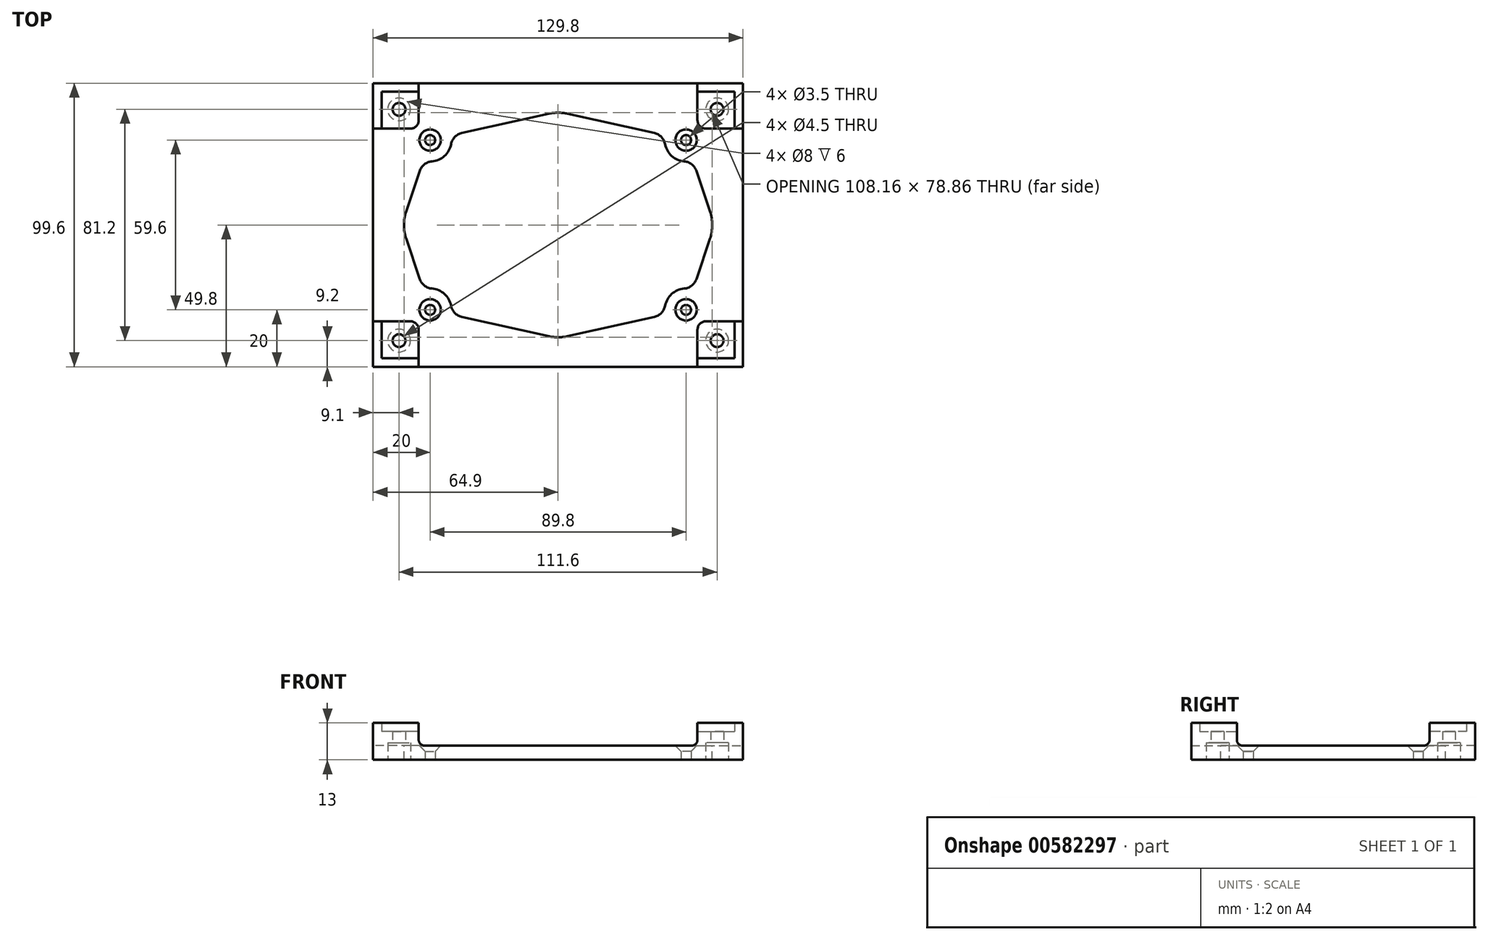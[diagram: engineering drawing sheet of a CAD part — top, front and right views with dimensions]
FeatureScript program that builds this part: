
annotation { "Feature Type Name" : "Feature", "Feature Type Description" : "" }
export const myFeature = defineFeature(function(context is Context, id is Id, definition is map)
    precondition{}
    {
        {
            var Q0;
            Q0=qCreatedBy(makeId("Top.planeOp"),FACE);
            var sketch = newSketch(context, id + "F0", { "sketchPlane" : qUnion([Q0])});
            skCircle(sketch, "E0", {"center": v(55.8, 40.6) * mm, "radius": 2.25 * mm});
            skCircle(sketch, "E1", {"center": v(55.8, 40.6) * mm, "radius": 4 * mm});
            skCircle(sketch, "E2", {"center": v(44.9, 29.8) * mm, "radius": 1.75 * mm});
            skLineSegment(sketch, "E3", {"start": v(0, 45.8) * mm, "end": v(60.9, 45.8) * mm, "construction": true});
            skLineSegment(sketch, "E4", {"start": v(60.9, 45.8) * mm, "end": v(60.9, 0) * mm, "construction": true});
            skLineSegment(sketch, "E5", {"start": v(48.9, 49.8) * mm, "end": v(48.9, 46.8) * mm});
            skLineSegment(sketch, "E6", {"start": v(48.9, 46.8) * mm, "end": v(61.9, 46.8) * mm});
            skLineSegment(sketch, "E7", {"start": v(61.9, 46.8) * mm, "end": v(61.9, 33.8) * mm});
            skLineSegment(sketch, "E8", {"start": v(61.9, 33.8) * mm, "end": v(64.9, 33.8) * mm});
            skLineSegment(sketch, "E9", {"start": v(64.9, 33.8) * mm, "end": v(64.9, 49.8) * mm});
            skLineSegment(sketch, "E10", {"start": v(64.9, 49.8) * mm, "end": v(48.9, 49.8) * mm});
            skLineSegment(sketch, "E11", {"start": v(48.9, 49.8) * mm, "end": v(0, 49.8) * mm});
            skLineSegment(sketch, "E12", {"start": v(64.9, 33.8) * mm, "end": v(64.9, 0) * mm});
            skLineSegment(sketch, "E13", {"start": v(44.9, 29.8) * mm, "end": v(0, 39.8) * mm});
            skLineSegment(sketch, "E14", {"start": v(44.9, 29.8) * mm, "end": v(54.9, 0) * mm});
            skArc(sketch, "E15", {"start": v(37.58, 31.43) * mm, "mid": v(39.88, 24.23) * mm, "end": v(47.29, 22.69) * mm});
            skLineSegment(sketch, "E16", {"start": v(0, 49.8) * mm, "end": v(0, 39.8) * mm});
            skLineSegment(sketch, "E17", {"start": v(54.9, 0) * mm, "end": v(64.9, 0) * mm});
            skLineSegment(sketch, "E18", {"start": v(48.9, 46.8) * mm, "end": v(48.9, 33.8) * mm});
            skLineSegment(sketch, "E19", {"start": v(48.9, 33.8) * mm, "end": v(61.9, 33.8) * mm});
            skSolve(sketch);
        }
        {
            var Q0;
            Q0=makeQuery(id+"F0.imprint","IMPRINT",FACE,{"disambiguationData":[TD([[makeQuery(id+"F0.imprint","IMPRINT",EDGE,{"derivedFrom":sQuery(id+"F0.wireOp",EDGE,"E5")}),-1.0]])]});
            var Q1;
            {var subQ5=sQuery(id+"F0.wireOp",EDGE,"E15");Q1=makeQuery(id+"F0.imprint","IMPRINT",FACE,{"disambiguationData":[TD([[makeQuery(id+"F0.imprint","IMPRINT",EDGE,{"derivedFrom":subQ5}),1.0]])]});}
            extrude(context, id + "F1", {"entities" : qUnion([Q0, Q1]), "depth" : 5 * mm, "offsetDistance" : 25 * mm});
        }
        {
            var Q0;
            Q0=makeQuery(id+"F0.imprint","IMPRINT",FACE,{"disambiguationData":[TD([[makeQuery(id+"F0.imprint","IMPRINT",EDGE,{"derivedFrom":sQuery(id+"F0.wireOp",EDGE,"E1")}),-1.0]])]});
            var Q1;
            Q1=makeQuery(id+"F0.imprint","IMPRINT",FACE,{"disambiguationData":[TD([[makeQuery(id+"F0.imprint","IMPRINT",EDGE,{"derivedFrom":sQuery(id+"F0.wireOp",EDGE,"E0")}),-1.0]])]});
            extrude(context, id + "F2", {"entities" : qUnion([Q0, Q1]), "operationType" : NewBodyOperationType.ADD, "depth" : 10 * mm, "offsetDistance" : 25 * mm});
        }
        {
            var Q0;
            Q0=makeQuery(id+"F0.imprint","IMPRINT",FACE,{"disambiguationData":[TD([[makeQuery(id+"F0.imprint","IMPRINT",EDGE,{"derivedFrom":sQuery(id+"F0.wireOp",EDGE,"E5")}),1.0]])]});
            extrude(context, id + "F3", {"entities" : qUnion([Q0]), "operationType" : NewBodyOperationType.ADD, "depth" : 13 * mm, "offsetDistance" : 25 * mm});
        }
        {
            var Q0;
            Q0=makeQuery(id+"F0.imprint","IMPRINT",FACE,{"disambiguationData":[TD([[makeQuery(id+"F0.imprint","IMPRINT",EDGE,{"derivedFrom":sQuery(id+"F0.wireOp",EDGE,"E0")}),-1.0]])]});
            extrude(context, id + "F4", {"entities" : qUnion([Q0]), "operationType" : NewBodyOperationType.REMOVE, "depth" : 6 * mm, "offsetDistance" : 25 * mm});
        }
        {
            var Q0;
            Q0=makeQuery(id+"F1.opExtrude","CAP_EDGE",EDGE,{"disambiguationData":[OSD([sQuery(id+"F0.wireOp",EDGE,"E2")])],"isStart":false});
            chamfer(context, id + "F5", {"entities" : qUnion([Q0]), "width" : 2 * mm, "tangentPropagation" : true});
        }
        {
            var Q0;
            Q0=makeQuery(id+"F2.opExtrude","SWEPT_EDGE",EDGE,{"disambiguationData":[OSD([sQuery(id+"F0.wireOp",EDGE,"E18"),sQuery(id+"F0.wireOp",EDGE,"E19")])]});
            fillet(context, id + "F6", {"entities" : qUnion([Q0]), "radius" : 3 * mm, "tangentPropagation" : true, "allowEdgeOverflow" : false});
        }
        {
            var Q0;
            {var subQ0=sQuery(id+"F0.wireOp",EDGE,"E19");var subQ1=sQuery(id+"F0.wireOp",EDGE,"E8");var subQ3=makeQuery(id+"F1.opExtrude","CAP_EDGE",EDGE,{"disambiguationData":[OSD([subQ1,subQ0])],"isStart":false});Q0=makeQuery(id+"F3.boolean.opBoolean","MERGE",EDGE,{"derivedFrom":[makeQuery(id+"F2.boolean.opBoolean","SPLIT",EDGE,{"disambiguationData":[topologyDisambiguationEdgeConnected([makeQuery(id+"F1.opExtrude","SWEPT_FACE",FACE,{"disambiguationData":[OSD([subQ1,subQ0])]})])],"derivedFrom":subQ3}),makeQuery(id+"F2.boolean.opBoolean","SPLIT",EDGE,{"disambiguationData":[topologyDisambiguationEdgeConnected([makeQuery(id+"F2.opExtrude","SWEPT_FACE",FACE,{"disambiguationData":[OSD([subQ0])]})])],"derivedFrom":subQ3})]});}
            var Q1;
            {var subQ0=sQuery(id+"F0.wireOp",EDGE,"E19");var subQ1=sQuery(id+"F0.wireOp",EDGE,"E18");Q1=makeQuery(id+"F6.opFillet","BLEND_EDGE",EDGE,{"blendedFrom":[makeQuery(id+"F2.opExtrude","SWEPT_EDGE",EDGE,{"disambiguationData":[OSD([subQ1,subQ0])]}),makeQuery(id+"F1.opExtrude","CAP_FACE",FACE,{"disambiguationData":[OSD([sQuery(id+"F0.wireOp",EDGE,"E2"),sQuery(id+"F0.wireOp",EDGE,"E5"),sQuery(id+"F0.wireOp",EDGE,"E8"),sQuery(id+"F0.wireOp",EDGE,"E11"),sQuery(id+"F0.wireOp",EDGE,"E12"),sQuery(id+"F0.wireOp",EDGE,"E13"),sQuery(id+"F0.wireOp",EDGE,"E14"),sQuery(id+"F0.wireOp",EDGE,"E15"),sQuery(id+"F0.wireOp",EDGE,"E16"),sQuery(id+"F0.wireOp",EDGE,"E17"),subQ1,subQ0])],"isStart":false})],"blendedInto":[makeQuery(id+"F1.opExtrude","CAP_FACE",FACE,{"disambiguationData":[OSD([sQuery(id+"F0.wireOp",EDGE,"E2"),sQuery(id+"F0.wireOp",EDGE,"E5"),sQuery(id+"F0.wireOp",EDGE,"E8"),sQuery(id+"F0.wireOp",EDGE,"E11"),sQuery(id+"F0.wireOp",EDGE,"E12"),sQuery(id+"F0.wireOp",EDGE,"E13"),sQuery(id+"F0.wireOp",EDGE,"E14"),sQuery(id+"F0.wireOp",EDGE,"E15"),sQuery(id+"F0.wireOp",EDGE,"E16"),sQuery(id+"F0.wireOp",EDGE,"E17"),subQ1,subQ0])],"isStart":false})]});}
            var Q2;
            {var subQ0=sQuery(id+"F0.wireOp",EDGE,"E18");var subQ1=sQuery(id+"F0.wireOp",EDGE,"E5");var subQ3=makeQuery(id+"F1.opExtrude","CAP_EDGE",EDGE,{"disambiguationData":[OSD([subQ1,subQ0])],"isStart":false});Q2=makeQuery(id+"F3.boolean.opBoolean","MERGE",EDGE,{"derivedFrom":[makeQuery(id+"F2.boolean.opBoolean","SPLIT",EDGE,{"disambiguationData":[topologyDisambiguationEdgeConnected([makeQuery(id+"F1.opExtrude","SWEPT_FACE",FACE,{"disambiguationData":[OSD([subQ1,subQ0])]})])],"derivedFrom":subQ3}),makeQuery(id+"F2.boolean.opBoolean","SPLIT",EDGE,{"disambiguationData":[topologyDisambiguationEdgeConnected([makeQuery(id+"F2.opExtrude","SWEPT_FACE",FACE,{"disambiguationData":[OSD([subQ0])]})])],"derivedFrom":subQ3})]});}
            fillet(context, id + "F7", {"entities" : qUnion([Q0, Q1, Q2]), "radius" : 2 * mm, "tangentPropagation" : true, "allowEdgeOverflow" : false});
        }
        {
            var Q0;
            Q0=makeQuery(id+"F1.opExtrude","SWEPT_EDGE",EDGE,{"disambiguationData":[OSD([sQuery(id+"F0.wireOp",EDGE,"E13"),sQuery(id+"F0.wireOp",EDGE,"E15")])]});
            var Q1;
            Q1=makeQuery(id+"F1.opExtrude","SWEPT_EDGE",EDGE,{"disambiguationData":[OSD([sQuery(id+"F0.wireOp",EDGE,"E14"),sQuery(id+"F0.wireOp",EDGE,"E15")])]});
            fillet(context, id + "F8", {"entities" : qUnion([Q0, Q1]), "radius" : 5 * mm, "tangentPropagation" : true, "allowEdgeOverflow" : false});
        }
        {
            var Q0;
            Q0=makeQuery(id+"F1.opExtrude","SWEPT_BODY",BODY,{"disambiguationData":[OSD([sQuery(id+"F0.wireOp",EDGE,"E2"),sQuery(id+"F0.wireOp",EDGE,"E5"),sQuery(id+"F0.wireOp",EDGE,"E8"),sQuery(id+"F0.wireOp",EDGE,"E11"),sQuery(id+"F0.wireOp",EDGE,"E12"),sQuery(id+"F0.wireOp",EDGE,"E13"),sQuery(id+"F0.wireOp",EDGE,"E14"),sQuery(id+"F0.wireOp",EDGE,"E15"),sQuery(id+"F0.wireOp",EDGE,"E16"),sQuery(id+"F0.wireOp",EDGE,"E17"),sQuery(id+"F0.wireOp",EDGE,"E18"),sQuery(id+"F0.wireOp",EDGE,"E19")])]});
            var Q1;
            Q1=makeQuery(id+"F1.opExtrude","SWEPT_FACE",FACE,{"disambiguationData":[OSD([sQuery(id+"F0.wireOp",EDGE,"E16")])]});
            mirror(context, id + "F9", {"operationType" : NewBodyOperationType.ADD, "entities" : qUnion([Q0]), "mirrorPlane" : qUnion([Q1])});
        }
        {
            var Q0;
            Q0=makeQuery(id+"F1.opExtrude","SWEPT_BODY",BODY,{"disambiguationData":[OSD([sQuery(id+"F0.wireOp",EDGE,"E2"),sQuery(id+"F0.wireOp",EDGE,"E5"),sQuery(id+"F0.wireOp",EDGE,"E8"),sQuery(id+"F0.wireOp",EDGE,"E11"),sQuery(id+"F0.wireOp",EDGE,"E12"),sQuery(id+"F0.wireOp",EDGE,"E13"),sQuery(id+"F0.wireOp",EDGE,"E14"),sQuery(id+"F0.wireOp",EDGE,"E15"),sQuery(id+"F0.wireOp",EDGE,"E16"),sQuery(id+"F0.wireOp",EDGE,"E17"),sQuery(id+"F0.wireOp",EDGE,"E18"),sQuery(id+"F0.wireOp",EDGE,"E19")])]});
            var Q1;
            Q1=makeQuery(id+"F1.opExtrude","SWEPT_FACE",FACE,{"disambiguationData":[OSD([sQuery(id+"F0.wireOp",EDGE,"E17")])]});
            mirror(context, id + "F10", {"operationType" : NewBodyOperationType.ADD, "entities" : qUnion([Q0]), "mirrorPlane" : qUnion([Q1])});
        }
        {
            var Q0;
            {var subQ0=makeQuery(id+"F1.opExtrude","SWEPT_EDGE",EDGE,{"disambiguationData":[OSD([sQuery(id+"F0.wireOp",EDGE,"E13"),sQuery(id+"F0.wireOp",EDGE,"E16")])]});Q0=makeQuery(id+"F9.boolean.opBoolean","MERGE",EDGE,{"derivedFrom":[subQ0,makeQuery(id+"F9.opPattern","COPY",EDGE,{"derivedFrom":subQ0,"instanceName":"1"})]});}
            var Q1;
            {var subQ0=makeQuery(id+"F1.opExtrude","SWEPT_EDGE",EDGE,{"disambiguationData":[OSD([sQuery(id+"F0.wireOp",EDGE,"E14"),sQuery(id+"F0.wireOp",EDGE,"E17")])]});Q1=makeQuery(id+"F10.boolean.opBoolean","MERGE",EDGE,{"derivedFrom":[subQ0,makeQuery(id+"F10.opPattern","COPY",EDGE,{"derivedFrom":subQ0,"instanceName":"1"})]});}
            var Q2;
            {var subQ0=makeQuery(id+"F1.opExtrude","SWEPT_EDGE",EDGE,{"disambiguationData":[OSD([sQuery(id+"F0.wireOp",EDGE,"E13"),sQuery(id+"F0.wireOp",EDGE,"E16")])]});Q2=makeQuery(id+"F10.opPattern","COPY",EDGE,{"derivedFrom":makeQuery(id+"F9.boolean.opBoolean","MERGE",EDGE,{"derivedFrom":[subQ0,makeQuery(id+"F9.opPattern","COPY",EDGE,{"derivedFrom":subQ0,"instanceName":"1"})]}),"instanceName":"1"});}
            var Q3;
            {var subQ0=makeQuery(id+"F9.opPattern","COPY",EDGE,{"derivedFrom":makeQuery(id+"F1.opExtrude","SWEPT_EDGE",EDGE,{"disambiguationData":[OSD([sQuery(id+"F0.wireOp",EDGE,"E14"),sQuery(id+"F0.wireOp",EDGE,"E17")])]}),"instanceName":"1"});Q3=makeQuery(id+"F10.boolean.opBoolean","MERGE",EDGE,{"derivedFrom":[subQ0,makeQuery(id+"F10.opPattern","COPY",EDGE,{"derivedFrom":subQ0,"instanceName":"1"})]});}
            fillet(context, id + "F11", {"entities" : qUnion([Q0, Q1, Q2, Q3]), "radius" : 15 * mm, "tangentPropagation" : true, "allowEdgeOverflow" : false});
        }
    });
